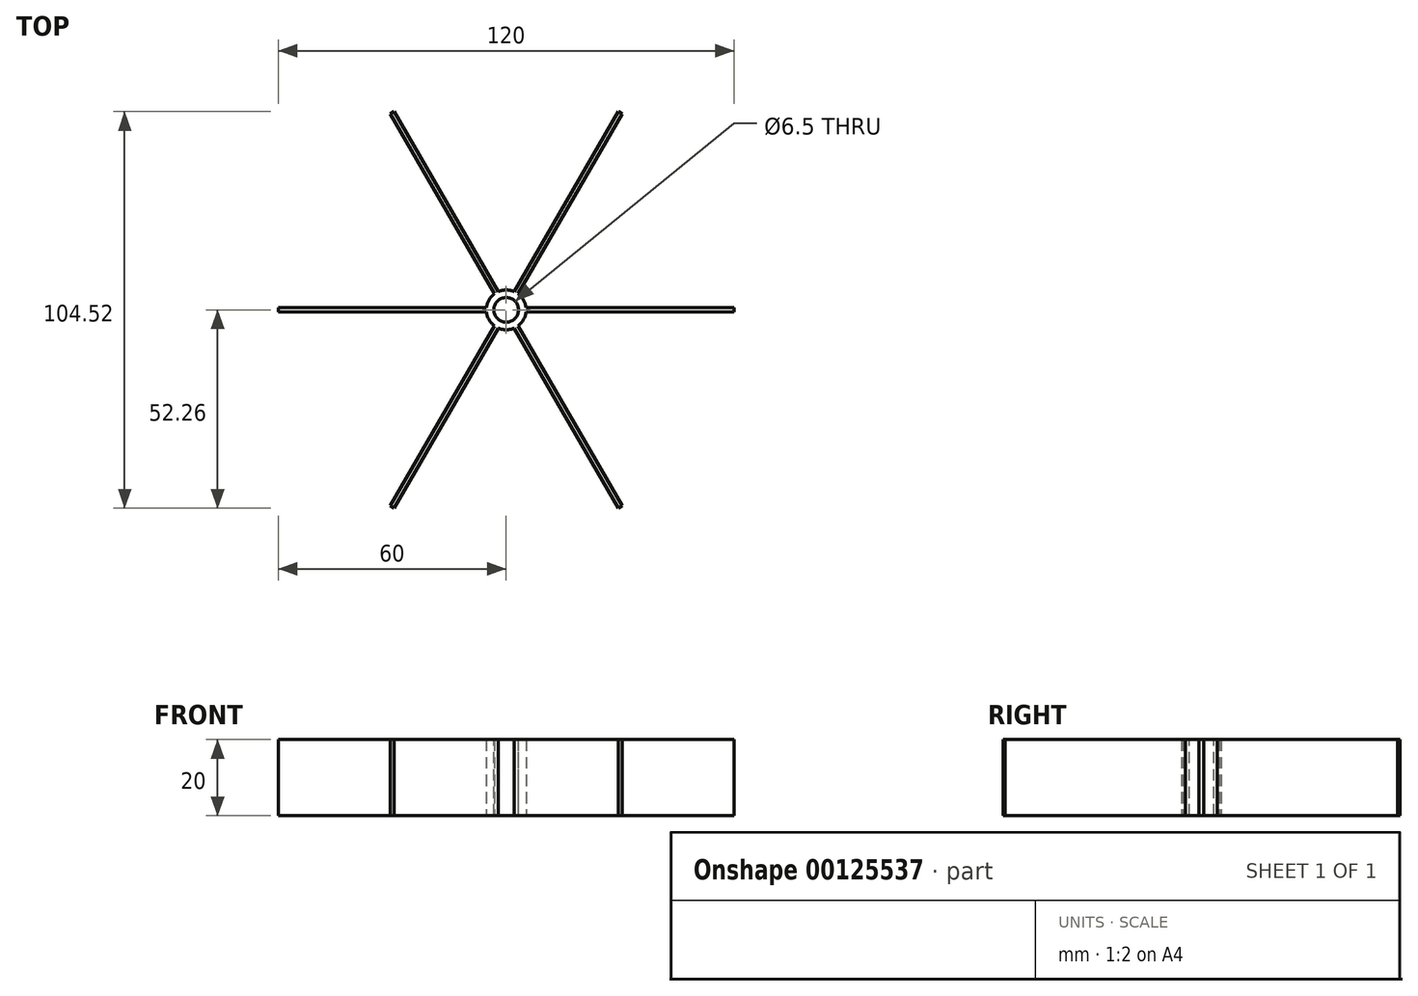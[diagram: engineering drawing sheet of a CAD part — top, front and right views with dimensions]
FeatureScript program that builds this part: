
annotation { "Feature Type Name" : "Feature", "Feature Type Description" : "" }
export const myFeature = defineFeature(function(context is Context, id is Id, definition is map)
    precondition{}
    {
        {
            var Q0;
            Q0=qCreatedBy(makeId("Top.planeOp"),FACE);
            var sketch = newSketch(context, id + "F0", { "sketchPlane" : qUnion([Q0])});
            skLineSegment(sketch, "E0.bottom", {"start": v(-60, 0.6) * mm, "end": v(0, 0.6) * mm});
            skLineSegment(sketch, "E0.top", {"start": v(-60, -0.6) * mm, "end": v(0, -0.6) * mm});
            skLineSegment(sketch, "E0.left", {"start": v(-60, 0.6) * mm, "end": v(-60, -0.6) * mm});
            skLineSegment(sketch, "E0.right", {"start": v(0, 0.6) * mm, "end": v(0, -0.6) * mm});
            skPoint(sketch, "E1", {"position": v(-60, 0) * mm});
            skPoint(sketch, "E2", {"position": v(0, 0) * mm});
            skPoint(sketch, "E3.1.0", {"position": v(-30, -51.96) * mm});
            skLineSegment(sketch, "E3.1.2", {"start": v(-29.48, -52.26) * mm, "end": v(0.52, -0.3) * mm});
            skLineSegment(sketch, "E3.1.3", {"start": v(-30.52, -51.66) * mm, "end": v(-0.52, 0.3) * mm});
            skLineSegment(sketch, "E3.1.4", {"start": v(-0.52, 0.3) * mm, "end": v(0.52, -0.3) * mm});
            skLineSegment(sketch, "E3.1.5", {"start": v(-30.52, -51.66) * mm, "end": v(-29.48, -52.26) * mm});
            skPoint(sketch, "E3.2.0", {"position": v(30, -51.96) * mm});
            skLineSegment(sketch, "E3.2.2", {"start": v(30.52, -51.66) * mm, "end": v(0.52, 0.3) * mm});
            skLineSegment(sketch, "E3.2.3", {"start": v(29.48, -52.26) * mm, "end": v(-0.52, -0.3) * mm});
            skLineSegment(sketch, "E3.2.4", {"start": v(-0.52, -0.3) * mm, "end": v(0.52, 0.3) * mm});
            skLineSegment(sketch, "E3.2.5", {"start": v(29.48, -52.26) * mm, "end": v(30.52, -51.66) * mm});
            skPoint(sketch, "E3.3.0", {"position": v(60, 0) * mm});
            skLineSegment(sketch, "E3.3.2", {"start": v(60, 0.6) * mm, "end": v(0, 0.6) * mm});
            skLineSegment(sketch, "E3.3.3", {"start": v(60, -0.6) * mm, "end": v(0, -0.6) * mm});
            skLineSegment(sketch, "E3.3.4", {"start": v(0, -0.6) * mm, "end": v(0, 0.6) * mm});
            skLineSegment(sketch, "E3.3.5", {"start": v(60, -0.6) * mm, "end": v(60, 0.6) * mm});
            skPoint(sketch, "E3.4.0", {"position": v(30, 51.96) * mm});
            skLineSegment(sketch, "E3.4.2", {"start": v(29.48, 52.26) * mm, "end": v(-0.52, 0.3) * mm});
            skLineSegment(sketch, "E3.4.3", {"start": v(30.52, 51.66) * mm, "end": v(0.52, -0.3) * mm});
            skLineSegment(sketch, "E3.4.4", {"start": v(0.52, -0.3) * mm, "end": v(-0.52, 0.3) * mm});
            skLineSegment(sketch, "E3.4.5", {"start": v(30.52, 51.66) * mm, "end": v(29.48, 52.26) * mm});
            skPoint(sketch, "E3.5.0", {"position": v(-30, 51.96) * mm});
            skLineSegment(sketch, "E3.5.2", {"start": v(-30.52, 51.66) * mm, "end": v(-0.52, -0.3) * mm});
            skLineSegment(sketch, "E3.5.3", {"start": v(-29.48, 52.26) * mm, "end": v(0.52, 0.3) * mm});
            skLineSegment(sketch, "E3.5.4", {"start": v(0.52, 0.3) * mm, "end": v(-0.52, -0.3) * mm});
            skLineSegment(sketch, "E3.5.5", {"start": v(-29.48, 52.26) * mm, "end": v(-30.52, 51.66) * mm});
            skCircle(sketch, "E4", {"center": v(0, 0) * mm, "radius": 5.25 * mm});
            skSolve(sketch);
        }
        {
            var Q0;
            Q0 = qSketchRegion(id + "F0", true);
            extrude(context, id + "F1", {"entities" : qUnion([Q0]), "depth" : 20 * mm});
        }
        {
            var Q0;
            Q0=makeQuery(id+"F1.opExtrude","CAP_FACE",FACE,{"disambiguationData":[OSD([sQuery(id+"F0.wireOp",EDGE,"E0.bottom"),sQuery(id+"F0.wireOp",EDGE,"E0.top"),sQuery(id+"F0.wireOp",EDGE,"E0.left"),sQuery(id+"F0.wireOp",EDGE,"E3.1.2"),sQuery(id+"F0.wireOp",EDGE,"E3.1.3"),sQuery(id+"F0.wireOp",EDGE,"E3.1.5"),sQuery(id+"F0.wireOp",EDGE,"E3.2.2"),sQuery(id+"F0.wireOp",EDGE,"E3.2.3"),sQuery(id+"F0.wireOp",EDGE,"E3.2.5"),sQuery(id+"F0.wireOp",EDGE,"E3.3.2"),sQuery(id+"F0.wireOp",EDGE,"E3.3.3"),sQuery(id+"F0.wireOp",EDGE,"E3.3.5"),sQuery(id+"F0.wireOp",EDGE,"E3.4.2"),sQuery(id+"F0.wireOp",EDGE,"E3.4.3"),sQuery(id+"F0.wireOp",EDGE,"E3.4.5"),sQuery(id+"F0.wireOp",EDGE,"E3.5.2"),sQuery(id+"F0.wireOp",EDGE,"E3.5.3"),sQuery(id+"F0.wireOp",EDGE,"E3.5.5"),sQuery(id+"F0.wireOp",EDGE,"E4")])],"isStart":false});
            var sketch = newSketch(context, id + "F2", { "sketchPlane" : qUnion([Q0])});
            skCircle(sketch, "E5", {"center": v(0, 0) * mm, "radius": 3.25 * mm});
            skSolve(sketch);
        }
        {
            var Q0;
            Q0=makeQuery(id+"F2.imprint","IMPRINT",FACE,{"disambiguationData":[TD([[makeQuery(id+"F2.imprint","IMPRINT",EDGE,{"derivedFrom":sQuery(id+"F2.wireOp",EDGE,"E5")}),1.0]])]});
            extrude(context, id + "F3", {"entities" : qUnion([Q0]), "operationType" : NewBodyOperationType.REMOVE, "endBound" : BoundingType.THROUGH_ALL, "oppositeDirection" : true, "depth" : 25 * mm});
        }
    });
